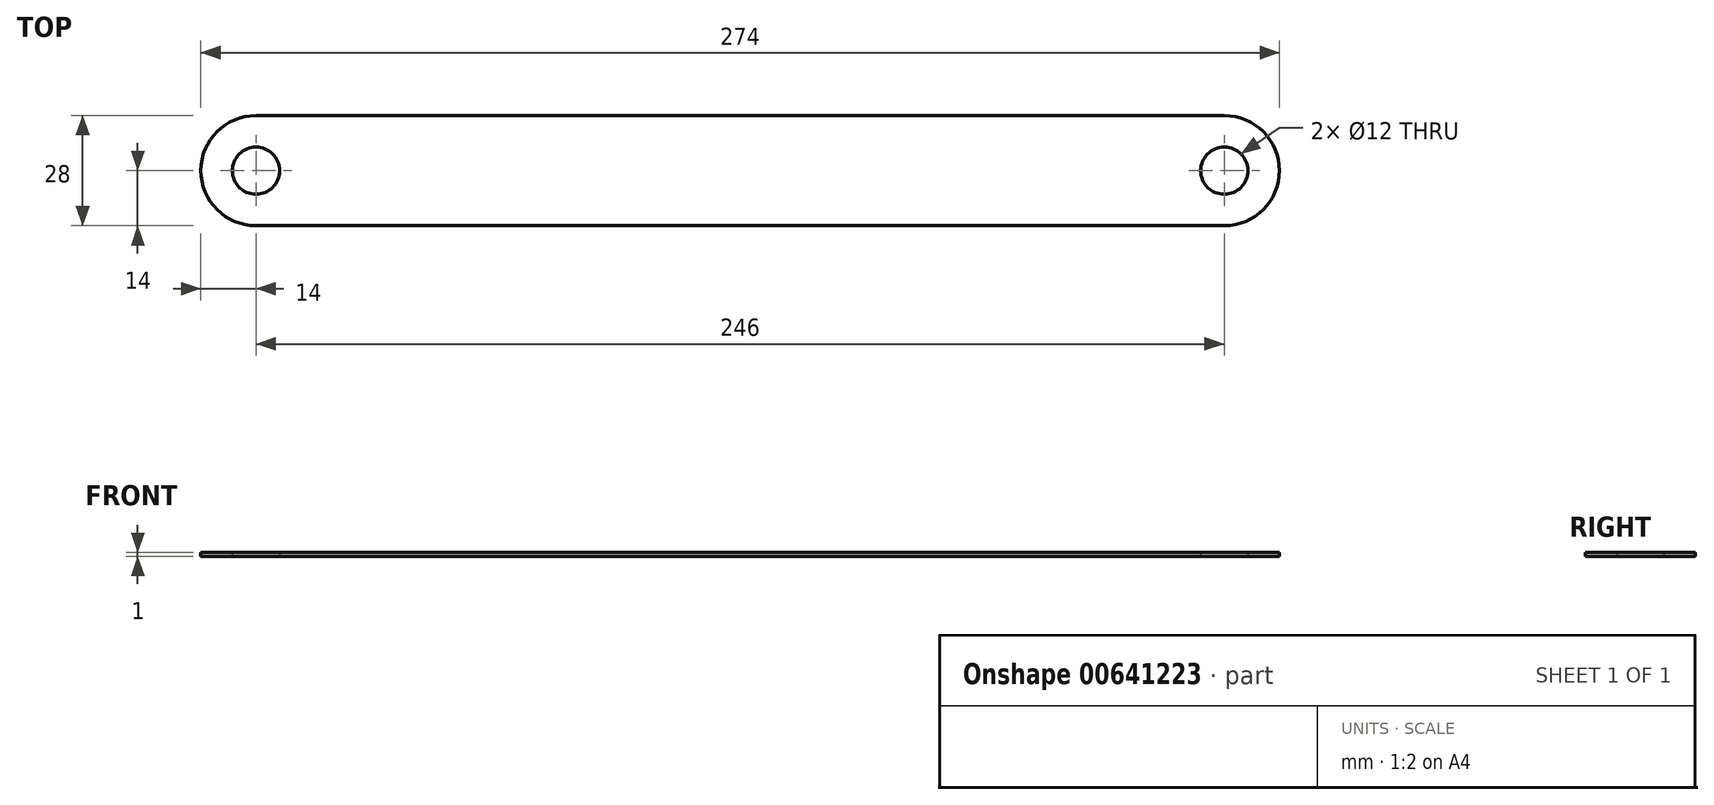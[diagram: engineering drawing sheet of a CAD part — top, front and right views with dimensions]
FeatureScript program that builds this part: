
annotation { "Feature Type Name" : "Feature", "Feature Type Description" : "" }
export const myFeature = defineFeature(function(context is Context, id is Id, definition is map)
    precondition{}
    {
        {
            var Q0;
            Q0=qCreatedBy(makeId("Top.planeOp"),FACE);
            var sketch = newSketch(context, id + "F0", { "sketchPlane" : qUnion([Q0])});
            skLineSegment(sketch, "E0.bottom", {"start": v(-123, 14) * mm, "end": v(123, 14) * mm});
            skLineSegment(sketch, "E0.top", {"start": v(-123, -14) * mm, "end": v(123, -14) * mm});
            skLineSegment(sketch, "E0.left", {"start": v(-137, 0) * mm, "end": v(-137, 0) * mm});
            skLineSegment(sketch, "E0.right", {"start": v(137, 0) * mm, "end": v(137, 0) * mm});
            skLineSegment(sketch, "E1", {"start": v(0, 0) * mm, "end": v(0, 14) * mm, "construction": true});
            skLineSegment(sketch, "E2", {"start": v(0, 0) * mm, "end": v(137, 0) * mm, "construction": true});
            skPoint(sketch, "E3.visualSharp", {"position": v(-137, 14) * mm});
            skArc(sketch, "E3.filletArc", {"start": v(-123, 14) * mm, "mid": v(-132.9, 9.9) * mm, "end": v(-137, 0) * mm});
            skPoint(sketch, "E4.visualSharp", {"position": v(-137, -14) * mm});
            skArc(sketch, "E4.filletArc", {"start": v(-137, 0) * mm, "mid": v(-132.9, -9.9) * mm, "end": v(-123, -14) * mm});
            skPoint(sketch, "E5.visualSharp", {"position": v(137, -14) * mm});
            skArc(sketch, "E5.filletArc", {"start": v(123, -14) * mm, "mid": v(132.9, -9.9) * mm, "end": v(137, 0) * mm});
            skPoint(sketch, "E6.visualSharp", {"position": v(137, 14) * mm});
            skArc(sketch, "E6.filletArc", {"start": v(137, 0) * mm, "mid": v(132.9, 9.9) * mm, "end": v(123, 14) * mm});
            skCircle(sketch, "E7", {"center": v(123, 0) * mm, "radius": 6 * mm});
            skCircle(sketch, "E8", {"center": v(-123, 0) * mm, "radius": 6 * mm});
            skSolve(sketch);
        }
        {
            var Q0;
            Q0 = qSketchRegion(id + "F0", true);
            extrude(context, id + "F1", {"entities" : qUnion([Q0]), "depth" : 1 * mm, "offsetDistance" : 25 * mm});
        }
    });
